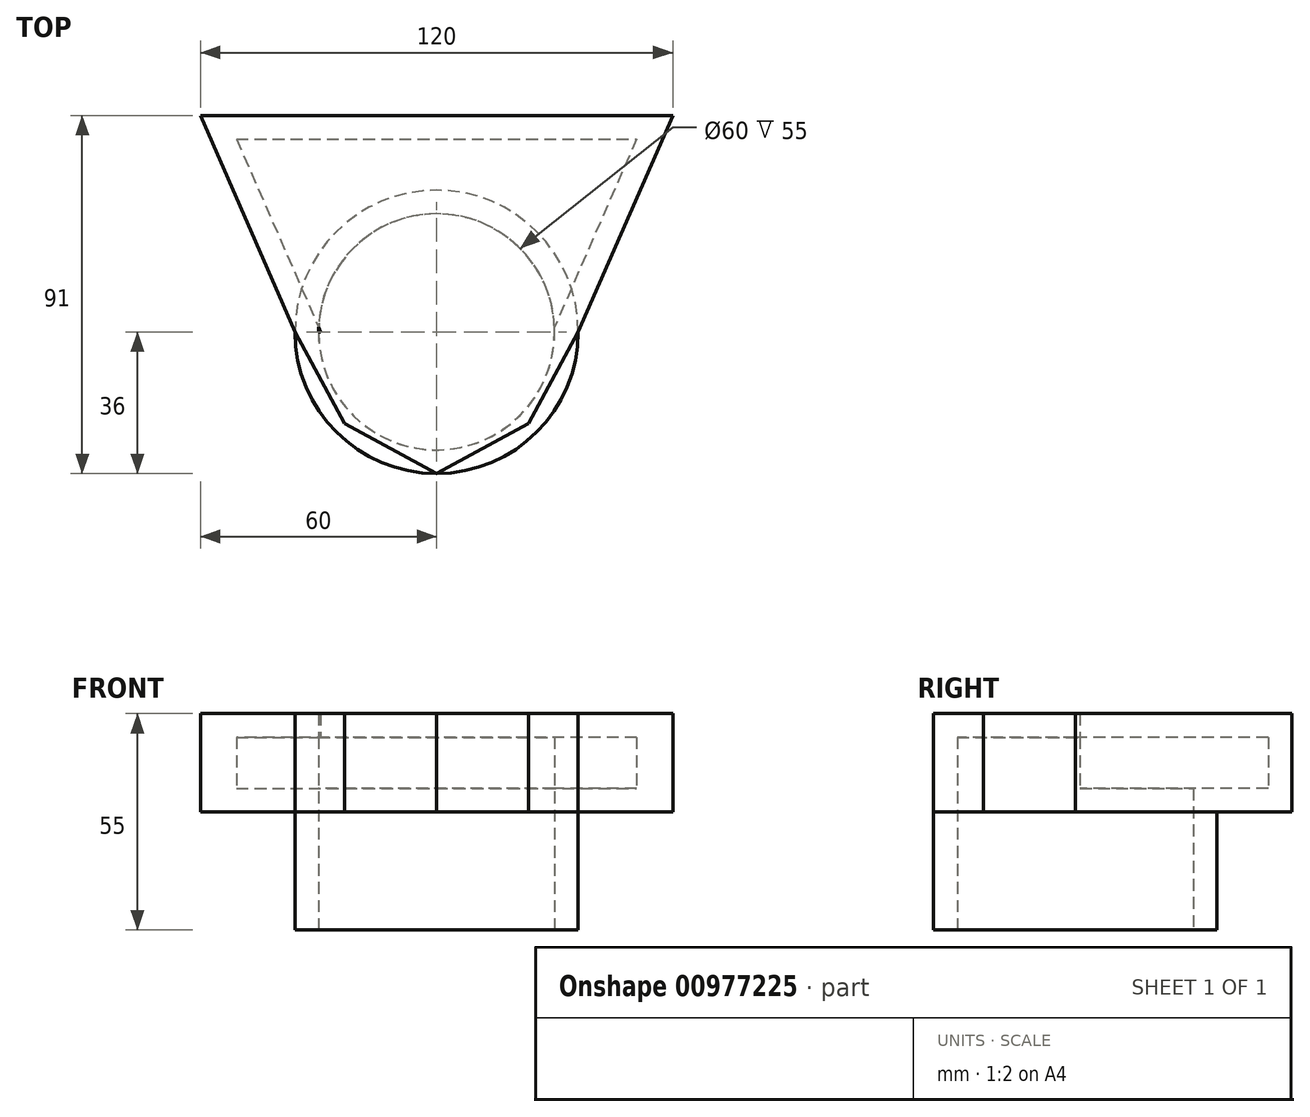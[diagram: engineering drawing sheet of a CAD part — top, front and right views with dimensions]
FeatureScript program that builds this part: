
annotation { "Feature Type Name" : "Feature", "Feature Type Description" : "" }
export const myFeature = defineFeature(function(context is Context, id is Id, definition is map)
    precondition{}
    {
        {
            var Q0;
            Q0=qCreatedBy(makeId("Top.planeOp"),FACE);
            var sketch = newSketch(context, id + "F0", { "sketchPlane" : qUnion([Q0])});
            skCircle(sketch, "E0", {"center": v(0, 0) * mm, "radius": 30 * mm});
            skCircle(sketch, "E1", {"center": v(0, 0) * mm, "radius": 36 * mm});
            skSolve(sketch);
        }
        {
            var Q0;
            Q0=makeQuery(id+"F0.imprint","IMPRINT",FACE,{"disambiguationData":[TD([[makeQuery(id+"F0.imprint","IMPRINT",EDGE,{"derivedFrom":sQuery(id+"F0.wireOp",EDGE,"E0")}),-1.0]])]});
            extrude(context, id + "F1", {"entities" : qUnion([Q0]), "depth" : 30 * mm, "offsetDistance" : 25 * mm});
        }
        {
            var Q0;
            Q0=makeQuery(id+"F1.opExtrude","CAP_FACE",FACE,{"disambiguationData":[OSD([sQuery(id+"F0.wireOp",EDGE,"E0"),sQuery(id+"F0.wireOp",EDGE,"E1")])],"isStart":false});
            cPlane(context, id + "F2", {"entities" : qUnion([Q0]), "cplaneType" : CPlaneType.OFFSET, "offset" : 0 * mm, "width" : 150 * mm, "height" : 150 * mm});
        }
        {
            var Q0;
            Q0=qCreatedBy(id+"F2.planeOp",FACE);
            var sketch = newSketch(context, id + "F3", { "sketchPlane" : qUnion([Q0])});
            skLineSegment(sketch, "E2", {"start": v(0, 0) * mm, "end": v(0, -36) * mm});
            skLineSegment(sketch, "E3", {"start": v(-29.45, 0) * mm, "end": v(-30, 0) * mm});
            skLineSegment(sketch, "E4", {"start": v(0, -36) * mm, "end": v(-23.33, -23.33) * mm});
            skLineSegment(sketch, "E5", {"start": v(-23.33, -23.33) * mm, "end": v(-36, 0) * mm});
            skLineSegment(sketch, "E6", {"start": v(0, 0) * mm, "end": v(0, 55) * mm});
            skLineSegment(sketch, "E7", {"start": v(0, 55) * mm, "end": v(-60, 55) * mm});
            skLineSegment(sketch, "E8", {"start": v(-36, 0) * mm, "end": v(-60, 55) * mm});
            skArc(sketch, "E9", {"start": v(-29.98, 1.2) * mm, "mid": v(20.79, -21.63) * mm, "end": v(0, 30) * mm});
            skLineSegment(sketch, "E10", {"start": v(0, 49) * mm, "end": v(-50.84, 49) * mm});
            skLineSegment(sketch, "E11", {"start": v(-50.84, 49) * mm, "end": v(-29.45, 0) * mm});
            skLineSegment(sketch, "E12", {"start": v(-29.45, 0) * mm, "end": v(0, -30) * mm});
            skLineSegment(sketch, "E13.MirrorCS", {"start": v(0, 55) * mm, "end": v(60, 55) * mm});
            skLineSegment(sketch, "E14.MirrorCS", {"start": v(0, 49) * mm, "end": v(50.84, 49) * mm});
            skLineSegment(sketch, "E15.MirrorCS", {"start": v(50.84, 49) * mm, "end": v(29.45, 0) * mm});
            skLineSegment(sketch, "E16.MirrorCS", {"start": v(36, 0) * mm, "end": v(60, 55) * mm});
            skLineSegment(sketch, "E17.MirrorCS", {"start": v(29.45, 0) * mm, "end": v(0, -30) * mm});
            skLineSegment(sketch, "E18.MirrorCS", {"start": v(0, -36) * mm, "end": v(23.33, -23.33) * mm});
            skLineSegment(sketch, "E19.MirrorCS", {"start": v(23.33, -23.33) * mm, "end": v(36, 0) * mm});
            skCircle(sketch, "E20", {"center": v(0, 0) * mm, "radius": 30 * mm});
            skSolve(sketch);
        }
        {
            var Q0;
            {var subQ3=sQuery(id+"F3.wireOp",EDGE,"E4");Q0=makeQuery(id+"F3.imprint","IMPRINT",FACE,{"disambiguationData":[TD([[makeQuery(id+"F3.imprint","IMPRINT",EDGE,{"derivedFrom":subQ3}),-1.0]])]});}
            var Q1;
            {var subQ6=sQuery(id+"F3.wireOp",EDGE,"E13.MirrorCS");Q1=makeQuery(id+"F3.imprint","IMPRINT",FACE,{"disambiguationData":[TD([[makeQuery(id+"F3.imprint","IMPRINT",EDGE,{"derivedFrom":subQ6}),-1.0]])]});}
            var Q2;
            {var subQ0=sQuery(id+"F3.wireOp",EDGE,"E10");Q2=makeQuery(id+"F3.imprint","IMPRINT",FACE,{"disambiguationData":[TD([[makeQuery(id+"F3.imprint","IMPRINT",EDGE,{"derivedFrom":subQ0}),1.0]])]});}
            var Q3;
            {var subQ0=sQuery(id+"F3.wireOp",EDGE,"E14.MirrorCS");Q3=makeQuery(id+"F3.imprint","IMPRINT",FACE,{"disambiguationData":[TD([[makeQuery(id+"F3.imprint","IMPRINT",EDGE,{"derivedFrom":subQ0}),-1.0]])]});}
            var Q4;
            {var subQ0=sQuery(id+"F3.wireOp",EDGE,"E17.MirrorCS");Q4=makeQuery(id+"F3.imprint","IMPRINT",FACE,{"disambiguationData":[TD([[makeQuery(id+"F3.imprint","IMPRINT",EDGE,{"derivedFrom":subQ0}),-1.0]])]});}
            var Q5;
            {var subQ0=sQuery(id+"F3.wireOp",EDGE,"E12");Q5=makeQuery(id+"F3.imprint","IMPRINT",FACE,{"disambiguationData":[TD([[makeQuery(id+"F3.imprint","IMPRINT",EDGE,{"derivedFrom":subQ0}),1.0]])]});}
            var Q6;
            {var subQ0=sQuery(id+"F3.wireOp",EDGE,"E3");Q6=makeQuery(id+"F3.imprint","IMPRINT",FACE,{"disambiguationData":[TD([[makeQuery(id+"F3.imprint","IMPRINT",EDGE,{"derivedFrom":subQ0}),1.0]])]});}
            var Q7;
            {var subQ0=sQuery(id+"F3.wireOp",EDGE,"E17.MirrorCS");Q7=makeQuery(id+"F3.imprint","IMPRINT",FACE,{"disambiguationData":[TD([[makeQuery(id+"F3.imprint","IMPRINT",EDGE,{"derivedFrom":subQ0}),1.0]])]});}
            extrude(context, id + "F4", {"entities" : qUnion([Q0, Q1, Q2, Q3, Q4, Q5, Q6, Q7]), "operationType" : NewBodyOperationType.ADD, "depth" : 25 * mm, "offsetDistance" : 25 * mm});
        }
        {
            var Q0;
            {var subQ0=sQuery(id+"F3.wireOp",EDGE,"E3");Q0=makeQuery(id+"F3.imprint","IMPRINT",FACE,{"disambiguationData":[TD([[makeQuery(id+"F3.imprint","IMPRINT",EDGE,{"derivedFrom":subQ0}),1.0]])]});}
            var Q1;
            {var subQ0=sQuery(id+"F3.wireOp",EDGE,"E12");Q1=makeQuery(id+"F3.imprint","IMPRINT",FACE,{"disambiguationData":[TD([[makeQuery(id+"F3.imprint","IMPRINT",EDGE,{"derivedFrom":subQ0}),1.0]])]});}
            var Q2;
            {var subQ0=sQuery(id+"F3.wireOp",EDGE,"E17.MirrorCS");Q2=makeQuery(id+"F3.imprint","IMPRINT",FACE,{"disambiguationData":[TD([[makeQuery(id+"F3.imprint","IMPRINT",EDGE,{"derivedFrom":subQ0}),-1.0]])]});}
            var Q3;
            {var subQ0=sQuery(id+"F3.wireOp",EDGE,"E17.MirrorCS");Q3=makeQuery(id+"F3.imprint","IMPRINT",FACE,{"disambiguationData":[TD([[makeQuery(id+"F3.imprint","IMPRINT",EDGE,{"derivedFrom":subQ0}),1.0]])]});}
            extrude(context, id + "F5", {"entities" : qUnion([Q0, Q1, Q2, Q3]), "operationType" : NewBodyOperationType.REMOVE, "depth" : 19 * mm, "offsetDistance" : 25 * mm});
        }
        {
            var Q0;
            {var subQ0=sQuery(id+"F3.wireOp",EDGE,"E10");Q0=makeQuery(id+"F3.imprint","IMPRINT",FACE,{"disambiguationData":[TD([[makeQuery(id+"F3.imprint","IMPRINT",EDGE,{"derivedFrom":subQ0}),1.0]])]});}
            var Q1;
            {var subQ0=sQuery(id+"F3.wireOp",EDGE,"E14.MirrorCS");Q1=makeQuery(id+"F3.imprint","IMPRINT",FACE,{"disambiguationData":[TD([[makeQuery(id+"F3.imprint","IMPRINT",EDGE,{"derivedFrom":subQ0}),-1.0]])]});}
            extrude(context, id + "F6", {"entities" : qUnion([Q0, Q1]), "operationType" : NewBodyOperationType.REMOVE, "depth" : 19 * mm, "offsetDistance" : 25 * mm});
        }
        {
            var Q0;
            {var subQ0=sQuery(id+"F3.wireOp",EDGE,"E14.MirrorCS");Q0=makeQuery(id+"F3.imprint","IMPRINT",FACE,{"disambiguationData":[TD([[makeQuery(id+"F3.imprint","IMPRINT",EDGE,{"derivedFrom":subQ0}),-1.0]])]});}
            var Q1;
            {var subQ0=sQuery(id+"F3.wireOp",EDGE,"E10");Q1=makeQuery(id+"F3.imprint","IMPRINT",FACE,{"disambiguationData":[TD([[makeQuery(id+"F3.imprint","IMPRINT",EDGE,{"derivedFrom":subQ0}),1.0]])]});}
            extrude(context, id + "F7", {"entities" : qUnion([Q0, Q1]), "operationType" : NewBodyOperationType.ADD, "depth" : 6 * mm, "offsetDistance" : 25 * mm});
        }
    });
